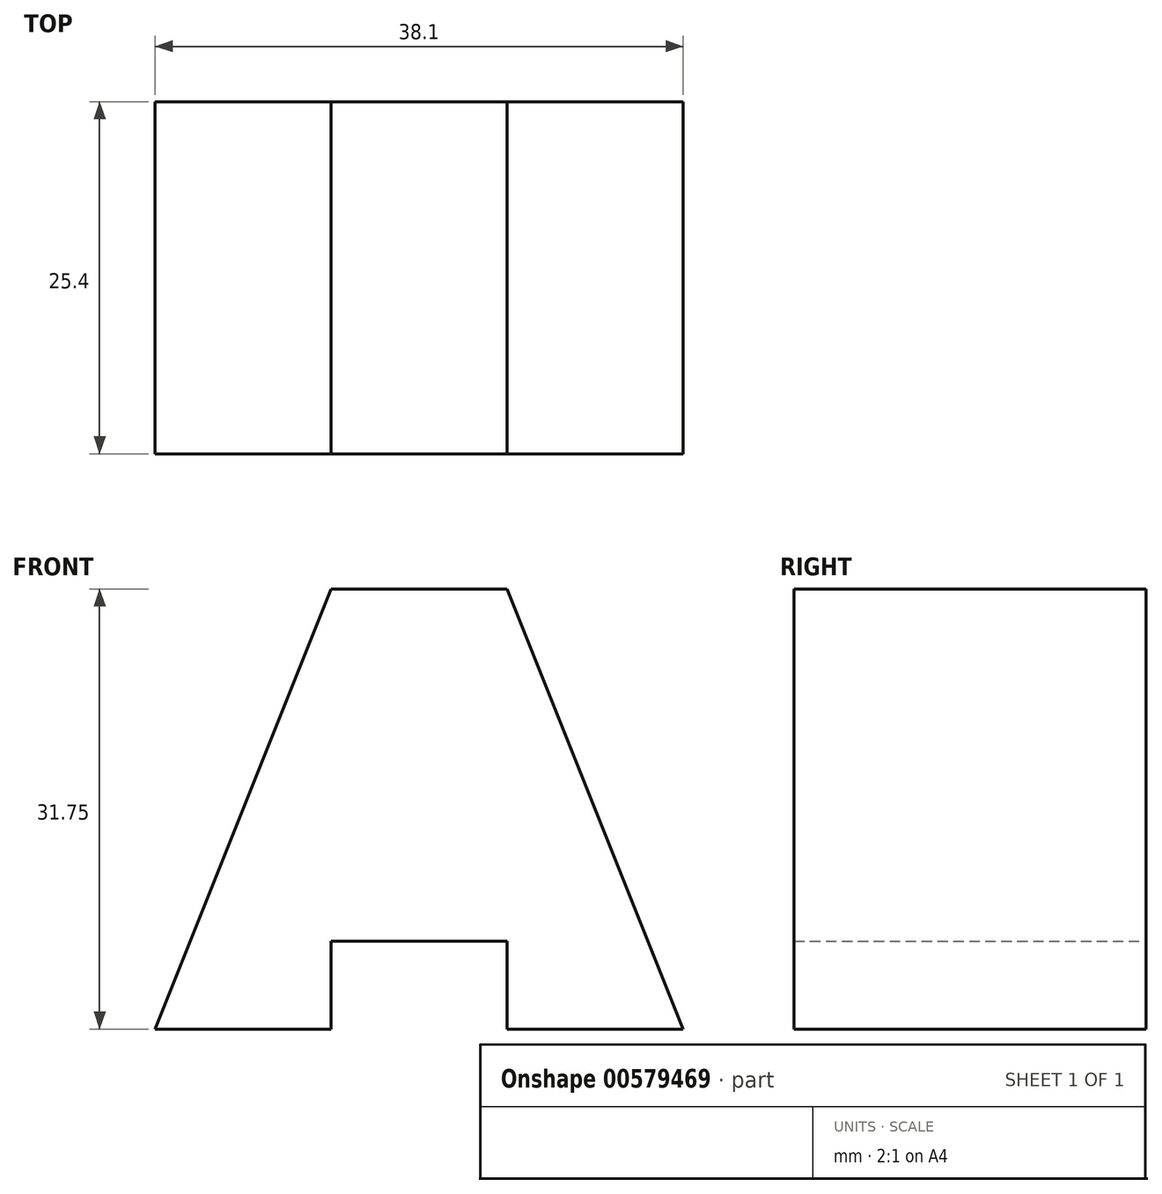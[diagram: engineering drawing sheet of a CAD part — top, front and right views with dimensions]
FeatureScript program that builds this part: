
annotation { "Feature Type Name" : "Feature", "Feature Type Description" : "" }
export const myFeature = defineFeature(function(context is Context, id is Id, definition is map)
    precondition{}
    {
        {
            var Q0;
            Q0=qCreatedBy(makeId("Front.planeOp"),FACE);
            var sketch = newSketch(context, id + "F0", { "sketchPlane" : qUnion([Q0])});
            skLineSegment(sketch, "E0", {"start": v(-44.42, 31.75) * mm, "end": v(-57.12, 0) * mm});
            skLineSegment(sketch, "E1", {"start": v(-57.12, 0) * mm, "end": v(-44.42, 0) * mm});
            skLineSegment(sketch, "E2", {"start": v(-44.42, 0) * mm, "end": v(-44.42, 6.35) * mm});
            skLineSegment(sketch, "E3", {"start": v(-44.42, 6.35) * mm, "end": v(-31.72, 6.35) * mm});
            skLineSegment(sketch, "E4", {"start": v(-31.72, 6.35) * mm, "end": v(-31.72, 0) * mm});
            skLineSegment(sketch, "E5", {"start": v(-31.72, 0) * mm, "end": v(-19.02, 0) * mm});
            skLineSegment(sketch, "E6", {"start": v(-19.02, 0) * mm, "end": v(-31.72, 31.75) * mm});
            skLineSegment(sketch, "E7", {"start": v(-31.72, 31.75) * mm, "end": v(-44.42, 31.75) * mm});
            skSolve(sketch);
        }
        {
            var Q0;
            Q0 = qSketchRegion(id + "F0", true);
            extrude(context, id + "F1", {"entities" : qUnion([Q0]), "depth" : 25.4 * mm, "offsetDistance" : 25.4 * mm});
        }
    });
